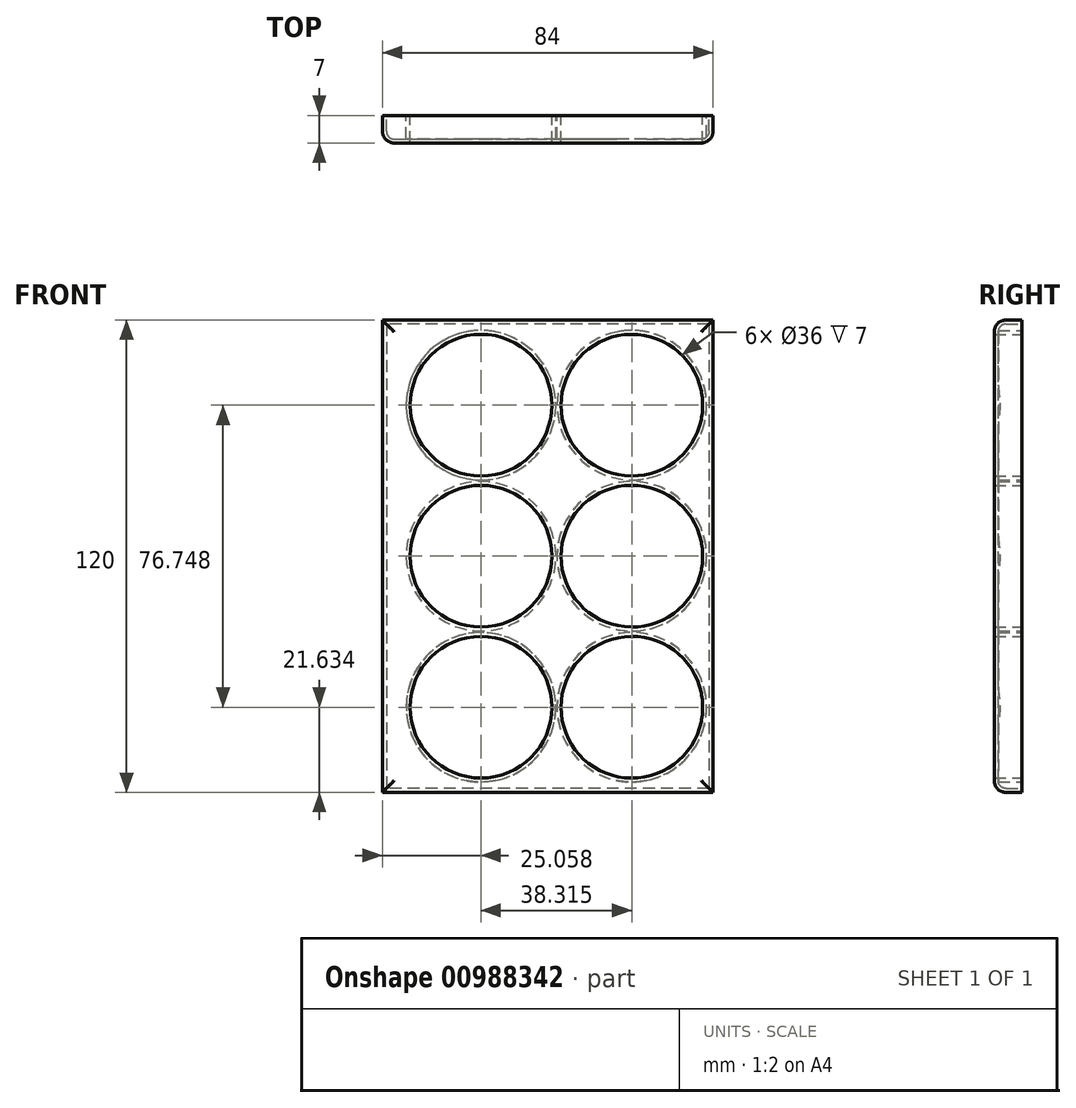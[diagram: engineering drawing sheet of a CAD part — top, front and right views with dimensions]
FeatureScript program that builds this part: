
annotation { "Feature Type Name" : "Feature", "Feature Type Description" : "" }
export const myFeature = defineFeature(function(context is Context, id is Id, definition is map)
    precondition{}
    {
        {
            var Q0;
            Q0=qCreatedBy(makeId("Front.planeOp"),FACE);
            var sketch = newSketch(context, id + "F0", { "sketchPlane" : qUnion([Q0])});
            skLineSegment(sketch, "E0.bottom", {"start": v(39.14, 62.73) * mm, "end": v(-40.86, 62.73) * mm});
            skLineSegment(sketch, "E0.top", {"start": v(39.14, -57.27) * mm, "end": v(-40.86, -57.27) * mm});
            skLineSegment(sketch, "E0.left", {"start": v(39.14, 62.73) * mm, "end": v(39.14, -57.27) * mm});
            skLineSegment(sketch, "E0.right", {"start": v(-40.86, 62.73) * mm, "end": v(-40.86, -57.27) * mm});
            skCircle(sketch, "E1", {"center": v(18.51, 2.74) * mm, "radius": 18 * mm});
            skCircle(sketch, "E2", {"center": v(18.51, -35.64) * mm, "radius": 18 * mm});
            skCircle(sketch, "E3.MirrorC", {"center": v(18.51, 41.11) * mm, "radius": 18 * mm});
            skLineSegment(sketch, "E4", {"start": v(-0.64, 2.74) * mm, "end": v(-0.64, -57.27) * mm});
            skLineSegment(sketch, "E5", {"start": v(-0.64, -57.27) * mm, "end": v(-0.64, 62.73) * mm});
            skCircle(sketch, "E6.MirrorC", {"center": v(-19.8, 41.11) * mm, "radius": 18 * mm});
            skCircle(sketch, "E7.MirrorC", {"center": v(-19.8, 2.74) * mm, "radius": 18 * mm});
            skCircle(sketch, "E8.MirrorC", {"center": v(-19.8, -35.64) * mm, "radius": 18 * mm});
            skLineSegment(sketch, "E9.bottom", {"start": v(-40.86, 62.73) * mm, "end": v(-44.86, 62.73) * mm});
            skLineSegment(sketch, "E9.top", {"start": v(-40.86, -57.27) * mm, "end": v(-44.86, -57.27) * mm});
            skLineSegment(sketch, "E9.right", {"start": v(-44.86, 62.73) * mm, "end": v(-44.86, -57.27) * mm});
            skSolve(sketch);
        }
        {
            var Q0;
            Q0=makeQuery(id+"F0.imprint","IMPRINT",FACE,{"disambiguationData":[TD([[makeQuery(id+"F0.imprint","IMPRINT",EDGE,{"derivedFrom":sQuery(id+"F0.wireOp",EDGE,"E0.right")}),-1.0]])]});
            var Q1;
            {var subQ2=sQuery(id+"F0.wireOp",EDGE,"E0.right");Q1=makeQuery(id+"F0.imprint","IMPRINT",FACE,{"disambiguationData":[TD([[makeQuery(id+"F0.imprint","IMPRINT",EDGE,{"derivedFrom":subQ2}),1.0]])]});}
            var Q2;
            {var subQ0=sQuery(id+"F0.wireOp",EDGE,"E0.left");Q2=makeQuery(id+"F0.imprint","IMPRINT",FACE,{"disambiguationData":[TD([[makeQuery(id+"F0.imprint","IMPRINT",EDGE,{"derivedFrom":subQ0}),-1.0]])]});}
            extrude(context, id + "F1", {"entities" : qUnion([Q0, Q1, Q2]), "depth" : 7 * mm, "offsetDistance" : 25 * mm});
        }
        {
            var Q0;
            Q0=makeQuery(id+"F1.opExtrude","CAP_EDGE",EDGE,{"disambiguationData":[OSD([sQuery(id+"F0.wireOp",EDGE,"E9.right")])],"isStart":false});
            var Q1;
            Q1=makeQuery(id+"F1.opExtrude","CAP_EDGE",EDGE,{"disambiguationData":[OSD([sQuery(id+"F0.wireOp",EDGE,"E0.top"),sQuery(id+"F0.wireOp",EDGE,"E9.top")])],"isStart":false});
            var Q2;
            Q2=makeQuery(id+"F1.opExtrude","CAP_EDGE",EDGE,{"disambiguationData":[OSD([sQuery(id+"F0.wireOp",EDGE,"E0.left")])],"isStart":false});
            var Q3;
            Q3=makeQuery(id+"F1.opExtrude","CAP_EDGE",EDGE,{"disambiguationData":[OSD([sQuery(id+"F0.wireOp",EDGE,"E0.bottom"),sQuery(id+"F0.wireOp",EDGE,"E9.bottom")])],"isStart":false});
            fillet(context, id + "F2", {"entities" : qUnion([Q0, Q1, Q2, Q3]), "radius" : 3 * mm, "tangentPropagation" : true, "allowEdgeOverflow" : false});
        }
        {
            var Q0;
            Q0=makeQuery(id+"F1.opExtrude","CAP_FACE",FACE,{"disambiguationData":[OSD([sQuery(id+"F0.wireOp",EDGE,"E0.bottom"),sQuery(id+"F0.wireOp",EDGE,"E0.top"),sQuery(id+"F0.wireOp",EDGE,"E0.left"),sQuery(id+"F0.wireOp",EDGE,"E1"),sQuery(id+"F0.wireOp",EDGE,"E2"),sQuery(id+"F0.wireOp",EDGE,"E3.MirrorC"),sQuery(id+"F0.wireOp",EDGE,"E6.MirrorC"),sQuery(id+"F0.wireOp",EDGE,"E7.MirrorC"),sQuery(id+"F0.wireOp",EDGE,"E8.MirrorC"),sQuery(id+"F0.wireOp",EDGE,"E9.bottom"),sQuery(id+"F0.wireOp",EDGE,"E9.top"),sQuery(id+"F0.wireOp",EDGE,"E9.right")])],"isStart":true});
            shell(context, id + "F3", {"entities" : qUnion([Q0]), "thickness" : 1 * mm});
        }
    });
